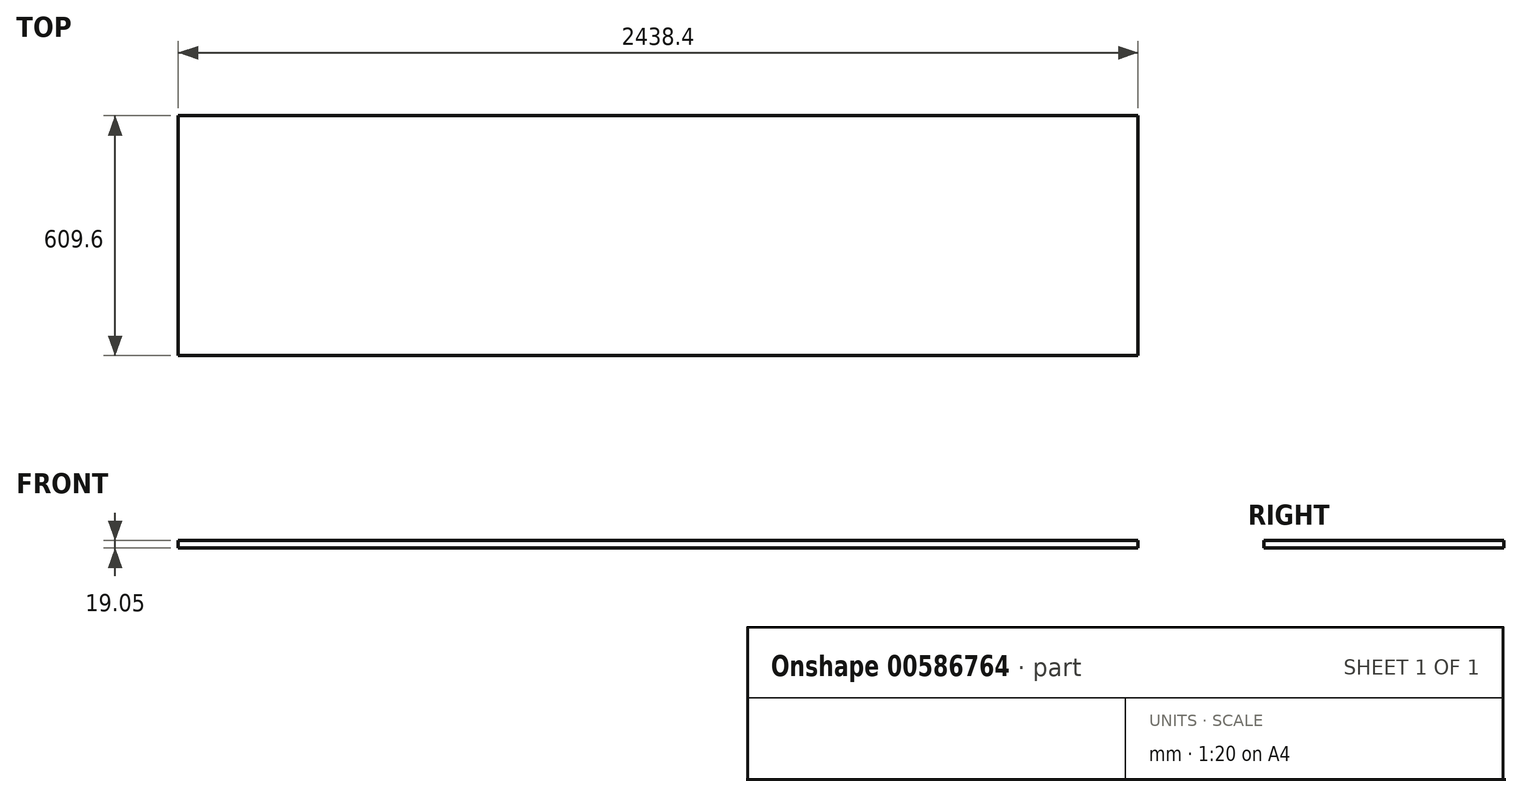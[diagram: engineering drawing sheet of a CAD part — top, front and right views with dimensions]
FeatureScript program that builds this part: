
annotation { "Feature Type Name" : "Feature", "Feature Type Description" : "" }
export const myFeature = defineFeature(function(context is Context, id is Id, definition is map)
    precondition{}
    {
        {
            var Q0;
            Q0=qCreatedBy(makeId("Top.planeOp"),FACE);
            var sketch = newSketch(context, id + "F0", { "sketchPlane" : qUnion([Q0])});
            skLineSegment(sketch, "E0.bottom", {"start": v(-1769.4, 591.7) * mm, "end": v(669, 591.7) * mm});
            skLineSegment(sketch, "E0.top", {"start": v(-1769.4, -17.9) * mm, "end": v(669, -17.9) * mm});
            skLineSegment(sketch, "E0.left", {"start": v(-1769.4, 591.7) * mm, "end": v(-1769.4, -17.9) * mm});
            skLineSegment(sketch, "E0.right", {"start": v(669, 591.7) * mm, "end": v(669, -17.9) * mm});
            skSolve(sketch);
        }
        {
            var Q0;
            Q0 = qSketchRegion(id + "F0", true);
            extrude(context, id + "F1", {"entities" : qUnion([Q0]), "depth" : 19.05 * mm, "offsetDistance" : 25.4 * mm});
        }
    });
